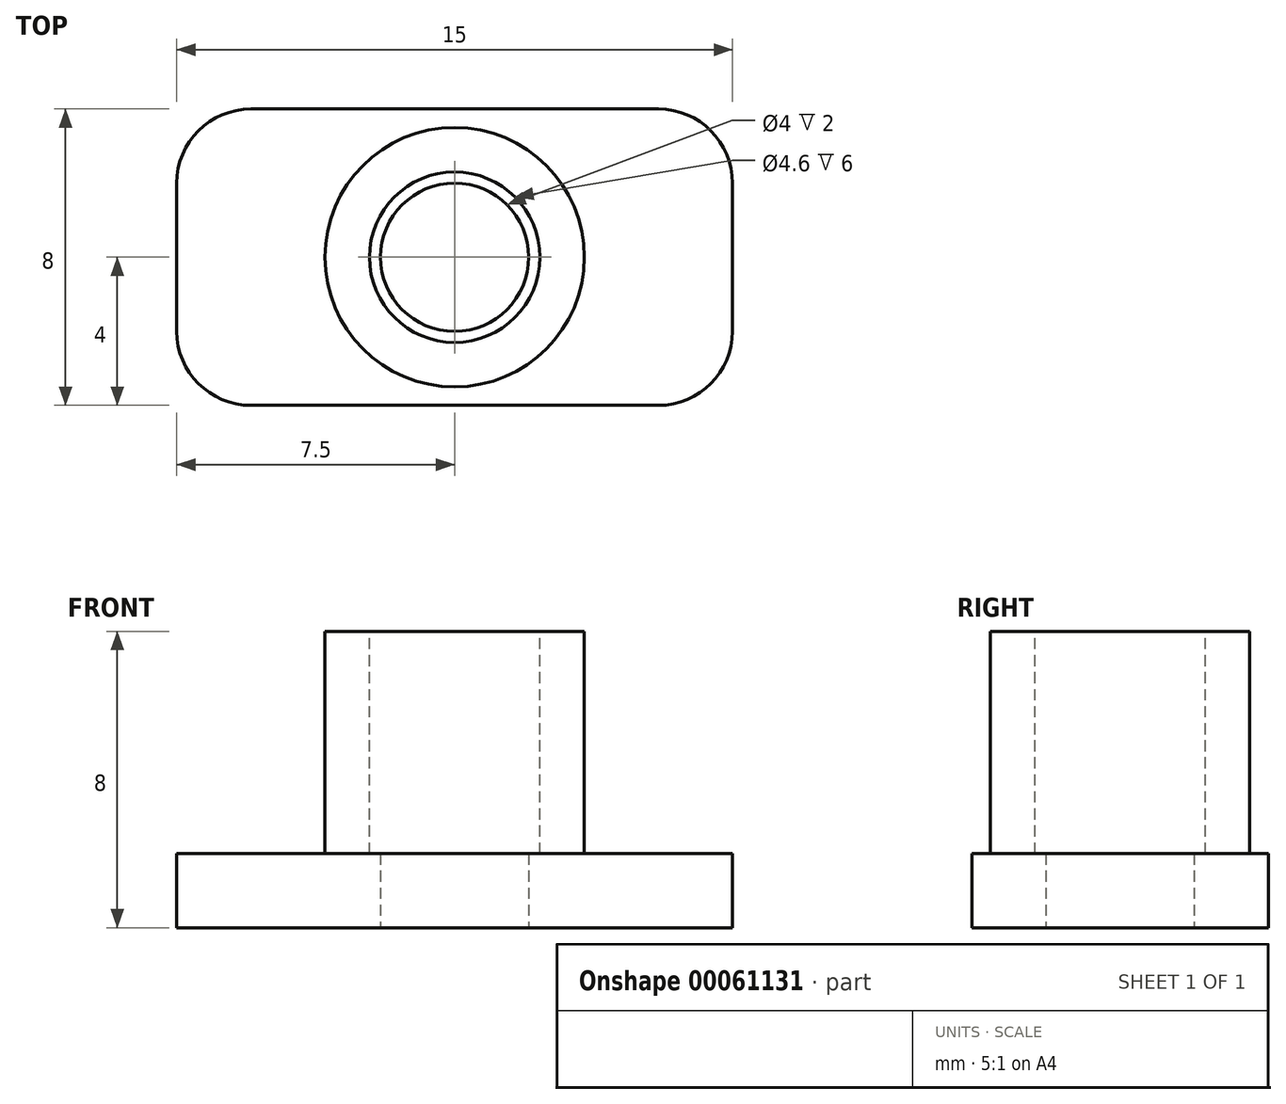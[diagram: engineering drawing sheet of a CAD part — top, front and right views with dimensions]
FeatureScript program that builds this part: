
annotation { "Feature Type Name" : "Feature", "Feature Type Description" : "" }
export const myFeature = defineFeature(function(context is Context, id is Id, definition is map)
    precondition{}
    {
        {
            var Q0;
            Q0=qCreatedBy(makeId("Top.planeOp"),FACE);
            var sketch = newSketch(context, id + "F0", { "sketchPlane" : qUnion([Q0])});
            skCircle(sketch, "E0", {"center": v(0, 0) * mm, "radius": 3.5 * mm});
            skCircle(sketch, "E1", {"center": v(0, 0) * mm, "radius": 2 * mm});
            skLineSegment(sketch, "E2.bottom", {"start": v(-5.5, 4) * mm, "end": v(5.5, 4) * mm});
            skLineSegment(sketch, "E2.top", {"start": v(-5.5, -4) * mm, "end": v(5.5, -4) * mm});
            skLineSegment(sketch, "E2.left", {"start": v(-7.5, 2) * mm, "end": v(-7.5, -2) * mm});
            skLineSegment(sketch, "E2.right", {"start": v(7.5, 2) * mm, "end": v(7.5, -2) * mm});
            skLineSegment(sketch, "E3", {"start": v(0, 0) * mm, "end": v(0, 12) * mm, "construction": true});
            skLineSegment(sketch, "E4", {"start": v(0, 0) * mm, "end": v(-11, 0) * mm, "construction": true});
            skPoint(sketch, "E5.visualSharp", {"position": v(-7.5, 4) * mm});
            skArc(sketch, "E5.filletArc", {"start": v(-5.5, 4) * mm, "mid": v(-6.91, 3.41) * mm, "end": v(-7.5, 2) * mm});
            skPoint(sketch, "E6.visualSharp", {"position": v(7.5, 4) * mm});
            skArc(sketch, "E6.filletArc", {"start": v(7.5, 2) * mm, "mid": v(6.91, 3.41) * mm, "end": v(5.5, 4) * mm});
            skPoint(sketch, "E7.visualSharp", {"position": v(7.5, -4) * mm});
            skArc(sketch, "E7.filletArc", {"start": v(5.5, -4) * mm, "mid": v(6.91, -3.41) * mm, "end": v(7.5, -2) * mm});
            skPoint(sketch, "E8.visualSharp", {"position": v(-7.5, -4) * mm});
            skArc(sketch, "E8.filletArc", {"start": v(-7.5, -2) * mm, "mid": v(-6.91, -3.41) * mm, "end": v(-5.5, -4) * mm});
            skSolve(sketch);
        }
        {
            var Q0;
            Q0=makeQuery(id+"F0.imprint","IMPRINT",FACE,{"disambiguationData":[TD([[makeQuery(id+"F0.imprint","IMPRINT",EDGE,{"derivedFrom":sQuery(id+"F0.wireOp",EDGE,"E0")}),1.0]])]});
            extrude(context, id + "F1", {"entities" : qUnion([Q0]), "depth" : 8 * mm});
        }
        {
            var Q0;
            Q0=makeQuery(id+"F1.opExtrude","CAP_FACE",FACE,{"disambiguationData":[OSD([sQuery(id+"F0.wireOp",EDGE,"E0"),sQuery(id+"F0.wireOp",EDGE,"E1")])],"isStart":false});
            var sketch = newSketch(context, id + "F2", { "sketchPlane" : qUnion([Q0])});
            skCircle(sketch, "E9.0", {"center": v(0, 0) * mm, "radius": 2 * mm});
            skCircle(sketch, "E10", {"center": v(0, 0) * mm, "radius": 2.3 * mm});
            skSolve(sketch);
        }
        {
            var Q0;
            Q0=makeQuery(id+"F2.imprint","IMPRINT",FACE,{"disambiguationData":[TD([[makeQuery(id+"F2.imprint","IMPRINT",EDGE,{"derivedFrom":sQuery(id+"F2.wireOp",EDGE,"E9.0")}),-1.0]])]});
            extrude(context, id + "F3", {"entities" : qUnion([Q0]), "operationType" : NewBodyOperationType.REMOVE, "oppositeDirection" : true, "depth" : 6 * mm});
        }
        {
            var Q0;
            Q0=qCreatedBy(makeId("Top.planeOp"),FACE);
            var sketch = newSketch(context, id + "F4", { "sketchPlane" : qUnion([Q0])});
            skCircle(sketch, "E11.0", {"center": v(0, 0) * mm, "radius": 2 * mm});
            skLineSegment(sketch, "E12.bottom", {"start": v(-5.5, 4) * mm, "end": v(5.5, 4) * mm});
            skLineSegment(sketch, "E12.top", {"start": v(-5.5, -4) * mm, "end": v(5.5, -4) * mm});
            skLineSegment(sketch, "E12.left", {"start": v(-7.5, 2) * mm, "end": v(-7.5, -2) * mm});
            skLineSegment(sketch, "E12.right", {"start": v(7.5, 2) * mm, "end": v(7.5, -2) * mm});
            skLineSegment(sketch, "E13", {"start": v(0, 0) * mm, "end": v(7.17, 0) * mm, "construction": true});
            skLineSegment(sketch, "E14", {"start": v(0, 0) * mm, "end": v(0, 4.45) * mm, "construction": true});
            skPoint(sketch, "E15.visualSharp", {"position": v(-7.5, 4) * mm});
            skArc(sketch, "E15.filletArc", {"start": v(-5.5, 4) * mm, "mid": v(-6.91, 3.41) * mm, "end": v(-7.5, 2) * mm});
            skPoint(sketch, "E16.visualSharp", {"position": v(7.5, 4) * mm});
            skArc(sketch, "E16.filletArc", {"start": v(7.5, 2) * mm, "mid": v(6.91, 3.41) * mm, "end": v(5.5, 4) * mm});
            skPoint(sketch, "E17.visualSharp", {"position": v(7.5, -4) * mm});
            skArc(sketch, "E17.filletArc", {"start": v(5.5, -4) * mm, "mid": v(6.91, -3.41) * mm, "end": v(7.5, -2) * mm});
            skPoint(sketch, "E18.visualSharp", {"position": v(-7.5, -4) * mm});
            skArc(sketch, "E18.filletArc", {"start": v(-7.5, -2) * mm, "mid": v(-6.91, -3.41) * mm, "end": v(-5.5, -4) * mm});
            skCircle(sketch, "E19.0", {"center": v(0, 0) * mm, "radius": 3.5 * mm});
            skCircle(sketch, "E20.0", {"center": v(0, 0) * mm, "radius": 2.3 * mm});
            skSolve(sketch);
        }
        {
            var Q0;
            Q0=makeQuery(id+"F4.imprint","IMPRINT",FACE,{"disambiguationData":[TD([[makeQuery(id+"F4.imprint","IMPRINT",EDGE,{"derivedFrom":sQuery(id+"F4.wireOp",EDGE,"E12.bottom")}),-1.0]])]});
            extrude(context, id + "F5", {"entities" : qUnion([Q0]), "operationType" : NewBodyOperationType.ADD, "depth" : 2 * mm});
        }
    });
